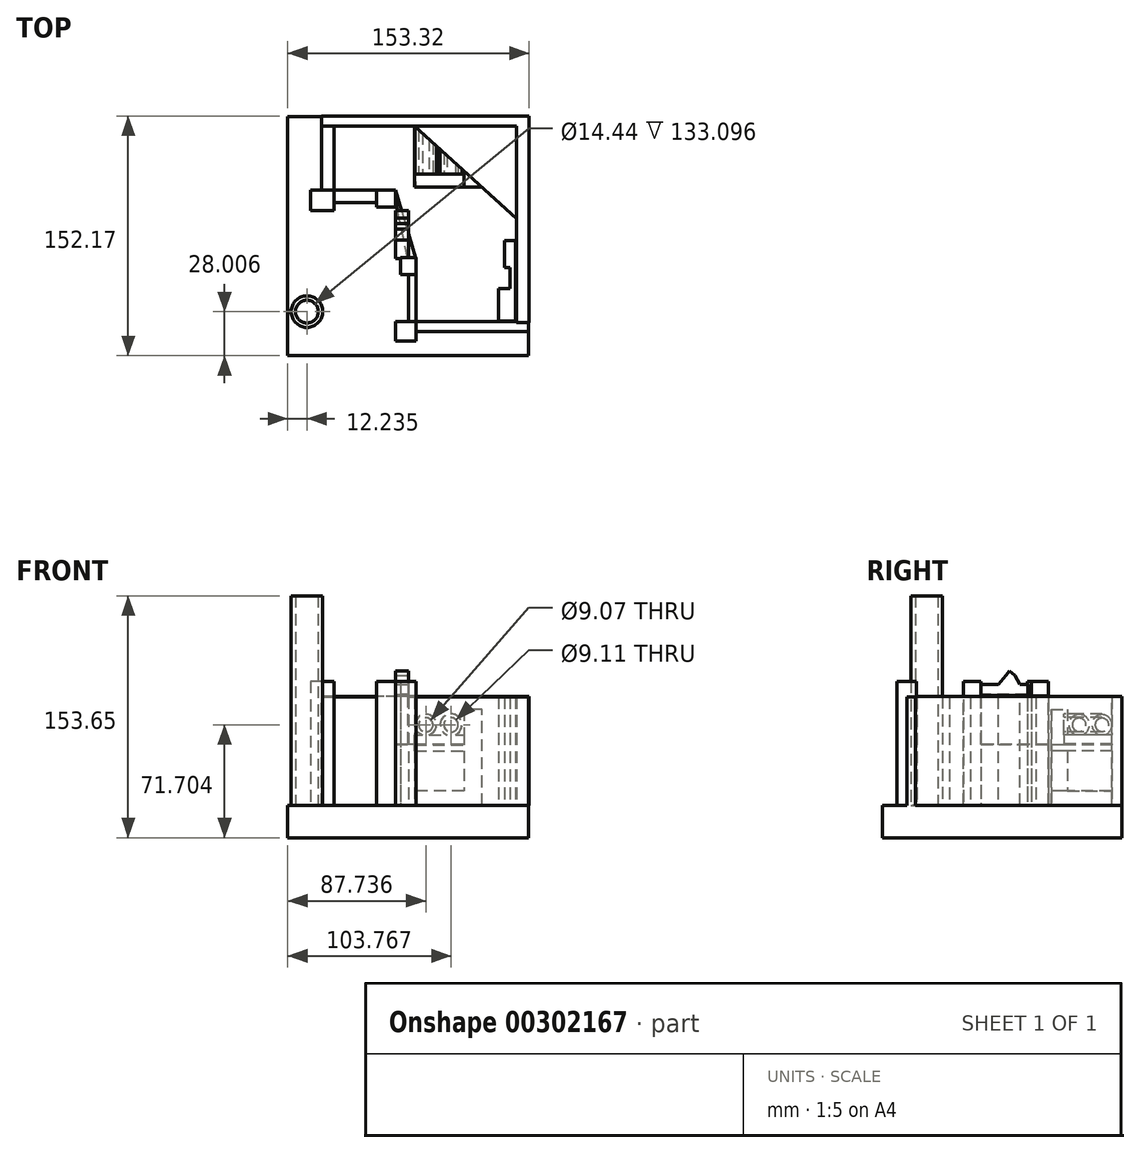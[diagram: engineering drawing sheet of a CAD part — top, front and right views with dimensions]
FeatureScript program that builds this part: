
annotation { "Feature Type Name" : "Feature", "Feature Type Description" : "" }
export const myFeature = defineFeature(function(context is Context, id is Id, definition is map)
    precondition{}
    {
        {
            var Q0;
            Q0=qCreatedBy(makeId("Front.planeOp"),FACE);
            var sketch = newSketch(context, id + "F0", { "sketchPlane" : qUnion([Q0])});
            skLineSegment(sketch, "E0.bottom", {"start": v(-76.66, 0) * mm, "end": v(76.37, 0) * mm});
            skLineSegment(sketch, "E0.top", {"start": v(-76.66, -20.55) * mm, "end": v(76.37, -20.55) * mm});
            skLineSegment(sketch, "E0.left", {"start": v(-76.66, 0) * mm, "end": v(-76.66, -20.55) * mm});
            skLineSegment(sketch, "E0.right", {"start": v(76.37, 0) * mm, "end": v(76.37, -20.55) * mm});
            skSolve(sketch);
        }
        {
            var Q0;
            Q0 = qSketchRegion(id + "F0", true);
            extrude(context, id + "F1", {"entities" : qUnion([Q0]), "depth" : 75.95 * mm, "hasSecondDirection" : true, "secondDirectionOppositeDirection" : true, "secondDirectionDepth" : 75.95 * mm});
        }
        {
            var Q0;
            Q0=makeQuery(id+"F1.opExtrude","SWEPT_FACE",FACE,{"disambiguationData":[OSD([sQuery(id+"F0.wireOp",EDGE,"E0.bottom")])]});
            var sketch = newSketch(context, id + "F2", { "sketchPlane" : qUnion([Q0])});
            skLineSegment(sketch, "E1", {"start": v(4.08, 69.8) * mm, "end": v(69.08, 69.8) * mm});
            skLineSegment(sketch, "E2", {"start": v(69.08, 69.8) * mm, "end": v(69.08, 10.93) * mm});
            skLineSegment(sketch, "E3", {"start": v(69.08, 10.93) * mm, "end": v(4.08, 69.8) * mm});
            skSolve(sketch);
        }
        {
            var Q0;
            Q0 = qSketchRegion(id + "F2", true);
            extrude(context, id + "F3", {"entities" : qUnion([Q0]), "operationType" : NewBodyOperationType.ADD, "depth" : 68.83 * mm});
        }
        {
            var Q0;
            Q0=qCreatedBy(makeId("Front.planeOp"),FACE);
            var sketch = newSketch(context, id + "F4", { "sketchPlane" : qUnion([Q0])});
            skLineSegment(sketch, "E4.bottom", {"start": v(4.08, 38.33) * mm, "end": v(35.27, 38.33) * mm});
            skLineSegment(sketch, "E4.top", {"start": v(4.08, 34.54) * mm, "end": v(35.27, 34.54) * mm});
            skLineSegment(sketch, "E4.left", {"start": v(4.08, 38.33) * mm, "end": v(4.08, 34.54) * mm});
            skLineSegment(sketch, "E4.right", {"start": v(35.27, 38.33) * mm, "end": v(35.27, 34.54) * mm});
            skLineSegment(sketch, "E5.bottom", {"start": v(68.79, 61.06) * mm, "end": v(35.27, 61.06) * mm});
            skLineSegment(sketch, "E5.top", {"start": v(68.79, 0) * mm, "end": v(35.27, 0) * mm});
            skLineSegment(sketch, "E5.left", {"start": v(68.79, 61.06) * mm, "end": v(68.79, 0) * mm});
            skLineSegment(sketch, "E5.right", {"start": v(35.27, 61.06) * mm, "end": v(35.27, 0) * mm});
            skLineSegment(sketch, "E6.bottom", {"start": v(35.27, 9.18) * mm, "end": v(4.66, 9.18) * mm});
            skLineSegment(sketch, "E6.top", {"start": v(35.27, 0) * mm, "end": v(4.66, 0) * mm});
            skLineSegment(sketch, "E6.left", {"start": v(35.27, 9.18) * mm, "end": v(35.27, 0) * mm});
            skLineSegment(sketch, "E6.right", {"start": v(4.66, 9.18) * mm, "end": v(4.66, 0) * mm});
            skSolve(sketch);
        }
        {
            var Q0;
            Q0 = qSketchRegion(id + "F4", true);
            extrude(context, id + "F5", {"entities" : qUnion([Q0]), "operationType" : NewBodyOperationType.ADD, "oppositeDirection" : true, "depth" : 70.1 * mm, "hasSecondDirection" : true, "secondDirectionOppositeDirection" : true, "secondDirectionDepth" : 31.24 * mm});
        }
        {
            var Q0;
            Q0=qCreatedBy(makeId("Front.planeOp"),FACE);
            var sketch = newSketch(context, id + "F6", { "sketchPlane" : qUnion([Q0])});
            skCircle(sketch, "E7", {"center": v(11.08, 51.15) * mm, "radius": 6.78 * mm});
            skCircle(sketch, "E8", {"center": v(11.08, 51.15) * mm, "radius": 4.53 * mm});
            skCircle(sketch, "E9", {"center": v(27.1, 51.15) * mm, "radius": 6.95 * mm});
            skCircle(sketch, "E10", {"center": v(27.1, 51.15) * mm, "radius": 4.55 * mm});
            skLineSegment(sketch, "E11.bottom", {"start": v(3.79, 44.74) * mm, "end": v(17.78, 44.74) * mm});
            skLineSegment(sketch, "E11.top", {"start": v(3.79, 38.91) * mm, "end": v(17.78, 38.91) * mm});
            skLineSegment(sketch, "E11.left", {"start": v(3.79, 44.74) * mm, "end": v(3.79, 38.91) * mm});
            skLineSegment(sketch, "E11.right", {"start": v(17.78, 44.74) * mm, "end": v(17.78, 38.91) * mm});
            skLineSegment(sketch, "E12.bottom", {"start": v(17.78, 44.74) * mm, "end": v(35.27, 44.74) * mm});
            skLineSegment(sketch, "E12.top", {"start": v(17.78, 38.91) * mm, "end": v(35.27, 38.91) * mm});
            skLineSegment(sketch, "E12.right", {"start": v(35.27, 44.74) * mm, "end": v(35.27, 38.91) * mm});
            skSolve(sketch);
        }
        {
            var Q0;
            Q0 = qSketchRegion(id + "F6", true);
            extrude(context, id + "F7", {"entities" : qUnion([Q0]), "operationType" : NewBodyOperationType.ADD, "oppositeDirection" : true, "depth" : 70.1 * mm, "hasSecondDirection" : true, "secondDirectionOppositeDirection" : true, "secondDirectionDepth" : 39.37 * mm});
        }
        {
            var Q0;
            Q0=qCreatedBy(makeId("Top.planeOp"),FACE);
            var sketch = newSketch(context, id + "F8", { "sketchPlane" : qUnion([Q0])});
            skLineSegment(sketch, "E13.bottom", {"start": v(68.79, 69.8) * mm, "end": v(76.66, 69.8) * mm});
            skLineSegment(sketch, "E13.top", {"start": v(68.79, -54.94) * mm, "end": v(76.66, -54.94) * mm});
            skLineSegment(sketch, "E13.left", {"start": v(68.79, 69.8) * mm, "end": v(68.79, -54.94) * mm});
            skLineSegment(sketch, "E13.right", {"start": v(76.66, 69.8) * mm, "end": v(76.66, -54.94) * mm});
            skLineSegment(sketch, "E14.bottom", {"start": v(76.66, 69.8) * mm, "end": v(-55.09, 69.8) * mm});
            skLineSegment(sketch, "E14.top", {"start": v(76.66, 76.22) * mm, "end": v(-55.09, 76.22) * mm});
            skLineSegment(sketch, "E14.left", {"start": v(76.66, 69.8) * mm, "end": v(76.66, 76.22) * mm});
            skLineSegment(sketch, "E14.right", {"start": v(-55.09, 69.8) * mm, "end": v(-55.09, 76.22) * mm});
            skSolve(sketch);
        }
        {
            var Q0;
            Q0 = qSketchRegion(id + "F8", true);
            extrude(context, id + "F9", {"entities" : qUnion([Q0]), "operationType" : NewBodyOperationType.ADD, "depth" : 69.1 * mm});
        }
        {
            var Q0;
            Q0=qCreatedBy(makeId("Top.planeOp"),FACE);
            var sketch = newSketch(context, id + "F10", { "sketchPlane" : qUnion([Q0])});
            skLineSegment(sketch, "E15.bottom", {"start": v(67.91, -2.77) * mm, "end": v(60.92, -2.77) * mm});
            skLineSegment(sketch, "E15.top", {"start": v(67.91, -19.97) * mm, "end": v(60.92, -19.97) * mm});
            skLineSegment(sketch, "E15.left", {"start": v(67.91, -2.77) * mm, "end": v(67.91, -19.97) * mm});
            skLineSegment(sketch, "E15.right", {"start": v(60.92, -2.77) * mm, "end": v(60.92, -19.97) * mm});
            skPoint(sketch, "E16.oppositeSnap0", {"position": v(64.42, -19.97) * mm});
            skLineSegment(sketch, "E16.bottom", {"start": v(67.91, -19.97) * mm, "end": v(64.42, -19.97) * mm});
            skLineSegment(sketch, "E16.top", {"start": v(67.91, -33.37) * mm, "end": v(64.42, -33.37) * mm});
            skLineSegment(sketch, "E16.left", {"start": v(67.91, -19.97) * mm, "end": v(67.91, -33.37) * mm});
            skLineSegment(sketch, "E16.right", {"start": v(64.42, -19.97) * mm, "end": v(64.42, -33.37) * mm});
            skLineSegment(sketch, "E17.bottom", {"start": v(67.91, -33.37) * mm, "end": v(57.13, -33.37) * mm});
            skLineSegment(sketch, "E17.top", {"start": v(67.91, -54.07) * mm, "end": v(57.13, -54.07) * mm});
            skLineSegment(sketch, "E17.left", {"start": v(67.91, -33.37) * mm, "end": v(67.91, -54.07) * mm});
            skLineSegment(sketch, "E17.right", {"start": v(57.13, -33.37) * mm, "end": v(57.13, -54.07) * mm});
            skSolve(sketch);
        }
        {
            var Q0;
            Q0 = qSketchRegion(id + "F10", true);
            extrude(context, id + "F11", {"entities" : qUnion([Q0]), "operationType" : NewBodyOperationType.ADD, "depth" : 68.83 * mm});
        }
        {
            var Q0;
            Q0=qCreatedBy(makeId("Top.planeOp"),FACE);
            var sketch = newSketch(context, id + "F12", { "sketchPlane" : qUnion([Q0])});
            skLineSegment(sketch, "E18.bottom", {"start": v(76.37, -54.36) * mm, "end": v(0, -54.36) * mm});
            skLineSegment(sketch, "E18.top", {"start": v(76.37, -60.48) * mm, "end": v(0, -60.48) * mm});
            skLineSegment(sketch, "E18.left", {"start": v(76.37, -54.36) * mm, "end": v(76.37, -60.48) * mm});
            skLineSegment(sketch, "E18.right", {"start": v(0, -54.36) * mm, "end": v(0, -60.48) * mm});
            skLineSegment(sketch, "E19.bottom", {"start": v(-55.09, 75.93) * mm, "end": v(-47.22, 75.93) * mm});
            skLineSegment(sketch, "E19.top", {"start": v(-55.09, 21.42) * mm, "end": v(-47.22, 21.42) * mm});
            skLineSegment(sketch, "E19.left", {"start": v(-55.09, 75.93) * mm, "end": v(-55.09, 21.42) * mm});
            skLineSegment(sketch, "E19.right", {"start": v(-47.22, 75.93) * mm, "end": v(-47.22, 21.42) * mm});
            skLineSegment(sketch, "E20.bottom", {"start": v(-47.22, 21.42) * mm, "end": v(-8.16, 21.42) * mm});
            skLineSegment(sketch, "E20.top", {"start": v(-47.22, 29.3) * mm, "end": v(-8.16, 29.3) * mm});
            skLineSegment(sketch, "E20.left", {"start": v(-47.22, 21.42) * mm, "end": v(-47.22, 29.3) * mm});
            skLineSegment(sketch, "E20.right", {"start": v(-8.16, 21.42) * mm, "end": v(-8.16, 29.3) * mm});
            skLineSegment(sketch, "E21.bottom", {"start": v(0, -54.36) * mm, "end": v(4.96, -54.36) * mm});
            skLineSegment(sketch, "E21.top", {"start": v(0, -15.3) * mm, "end": v(4.96, -15.3) * mm});
            skLineSegment(sketch, "E21.left", {"start": v(0, -54.36) * mm, "end": v(0, -15.3) * mm});
            skLineSegment(sketch, "E21.right", {"start": v(4.96, -54.36) * mm, "end": v(4.96, -15.3) * mm});
            skSolve(sketch);
        }
        {
            var Q0;
            Q0 = qSketchRegion(id + "F12", true);
            extrude(context, id + "F13", {"entities" : qUnion([Q0]), "operationType" : NewBodyOperationType.ADD, "depth" : 68.83 * mm});
        }
        {
            var Q0;
            Q0=makeQuery(id+"F1.opExtrude","SWEPT_FACE",FACE,{"disambiguationData":[OSD([sQuery(id+"F0.wireOp",EDGE,"E0.bottom")])]});
            var sketch = newSketch(context, id + "F14", { "sketchPlane" : qUnion([Q0])});
            skLineSegment(sketch, "E22", {"start": v(-8.16, 29.3) * mm, "end": v(4.96, -15.3) * mm});
            skLineSegment(sketch, "E23", {"start": v(0, -15.3) * mm, "end": v(-8.16, 21.42) * mm});
            skLineSegment(sketch, "E24", {"start": v(-8.16, 21.42) * mm, "end": v(-8.16, 29.3) * mm});
            skLineSegment(sketch, "E25", {"start": v(0, -15.3) * mm, "end": v(4.96, -15.3) * mm});
            skSolve(sketch);
        }
        {
            var Q0;
            Q0 = qSketchRegion(id + "F14", true);
            extrude(context, id + "F15", {"entities" : qUnion([Q0]), "operationType" : NewBodyOperationType.ADD, "depth" : 69.6 * mm, "hasSecondDirection" : true, "secondDirectionOppositeDirection" : false, "secondDirectionDepth" : 38.6 * mm});
        }
        {
            var Q0;
            Q0=makeQuery(id+"F1.opExtrude","SWEPT_FACE",FACE,{"disambiguationData":[OSD([sQuery(id+"F0.wireOp",EDGE,"E0.bottom")])]});
            var sketch = newSketch(context, id + "F16", { "sketchPlane" : qUnion([Q0])});
            skLineSegment(sketch, "E26.bottom", {"start": v(-4.84, -13.5) * mm, "end": v(4.96, -13.5) * mm});
            skLineSegment(sketch, "E26.top", {"start": v(-4.84, -24.42) * mm, "end": v(4.96, -24.42) * mm});
            skLineSegment(sketch, "E26.left", {"start": v(-4.84, -13.5) * mm, "end": v(-4.84, -24.42) * mm});
            skLineSegment(sketch, "E26.right", {"start": v(4.96, -13.5) * mm, "end": v(4.96, -24.42) * mm});
            skLineSegment(sketch, "E27.bottom", {"start": v(-8.16, 29.3) * mm, "end": v(-20.3, 29.3) * mm});
            skLineSegment(sketch, "E27.top", {"start": v(-8.16, 18.46) * mm, "end": v(-20.3, 18.46) * mm});
            skLineSegment(sketch, "E27.left", {"start": v(-8.16, 29.3) * mm, "end": v(-8.16, 18.46) * mm});
            skLineSegment(sketch, "E27.right", {"start": v(-20.3, 29.3) * mm, "end": v(-20.3, 18.46) * mm});
            skLineSegment(sketch, "E28.bottom", {"start": v(-47.22, 29.3) * mm, "end": v(-62.15, 29.3) * mm});
            skLineSegment(sketch, "E28.top", {"start": v(-47.22, 16.2) * mm, "end": v(-62.15, 16.2) * mm});
            skLineSegment(sketch, "E28.left", {"start": v(-47.22, 29.3) * mm, "end": v(-47.22, 16.2) * mm});
            skLineSegment(sketch, "E28.right", {"start": v(-62.15, 29.3) * mm, "end": v(-62.15, 16.2) * mm});
            skLineSegment(sketch, "E29.bottom", {"start": v(4.96, -54.36) * mm, "end": v(-8.16, -54.36) * mm});
            skLineSegment(sketch, "E29.top", {"start": v(4.96, -66.67) * mm, "end": v(-8.16, -66.67) * mm});
            skLineSegment(sketch, "E29.left", {"start": v(4.96, -54.36) * mm, "end": v(4.96, -66.67) * mm});
            skLineSegment(sketch, "E29.right", {"start": v(-8.16, -54.36) * mm, "end": v(-8.16, -66.67) * mm});
            skSolve(sketch);
        }
        {
            var Q0;
            Q0 = qSketchRegion(id + "F16", true);
            extrude(context, id + "F17", {"entities" : qUnion([Q0]), "operationType" : NewBodyOperationType.ADD, "depth" : 78.74 * mm});
        }
        {
            var Q0;
            Q0=qCreatedBy(makeId("Right.planeOp"),FACE);
            var sketch = newSketch(context, id + "F18", { "sketchPlane" : qUnion([Q0])});
            skLineSegment(sketch, "E30", {"start": v(16.16, 76.9) * mm, "end": v(11.38, 76.9) * mm});
            skLineSegment(sketch, "E31", {"start": v(11.38, 76.9) * mm, "end": v(8, 82.53) * mm});
            skLineSegment(sketch, "E32", {"start": v(8, 82.53) * mm, "end": v(4.63, 85.34) * mm});
            skLineSegment(sketch, "E33", {"start": v(4.63, 85.34) * mm, "end": v(2.28, 82.53) * mm});
            skLineSegment(sketch, "E34", {"start": v(2.28, 82.53) * mm, "end": v(-2.41, 76.9) * mm});
            skLineSegment(sketch, "E35", {"start": v(-2.41, 76.9) * mm, "end": v(-14.23, 76.9) * mm});
            skLineSegment(sketch, "E36", {"start": v(-14.23, 76.9) * mm, "end": v(-14.23, 70.42) * mm});
            skLineSegment(sketch, "E37", {"start": v(-14.23, 70.42) * mm, "end": v(15.88, 70.42) * mm});
            skLineSegment(sketch, "E38", {"start": v(15.88, 70.42) * mm, "end": v(16.16, 76.9) * mm});
            skSolve(sketch);
        }
        {
            var Q0;
            Q0 = qSketchRegion(id + "F18", true);
            extrude(context, id + "F19", {"entities" : qUnion([Q0]), "operationType" : NewBodyOperationType.ADD, "oppositeDirection" : true, "depth" : 8.13 * mm});
        }
        {
            var Q0;
            Q0=qCreatedBy(makeId("Top.planeOp"),FACE);
            var sketch = newSketch(context, id + "F20", { "sketchPlane" : qUnion([Q0])});
            skCircle(sketch, "E39", {"center": v(-64.42, -47.94) * mm, "radius": 10.03 * mm});
            skCircle(sketch, "E40", {"center": v(-64.42, -47.94) * mm, "radius": 7.22 * mm});
            skSolve(sketch);
        }
        {
            var Q0;
            Q0 = qSketchRegion(id + "F20", true);
            extrude(context, id + "F21", {"entities" : qUnion([Q0]), "operationType" : NewBodyOperationType.ADD, "depth" : 133.1 * mm});
        }
        {
            var Q0;
            Q0=qCreatedBy(makeId("Right.planeOp"),FACE);
            var sketch = newSketch(context, id + "F22", { "sketchPlane" : qUnion([Q0])});
            skLineSegment(sketch, "E41.bottom", {"start": v(16.3, 76.93) * mm, "end": v(15.26, 76.93) * mm});
            skLineSegment(sketch, "E41.top", {"start": v(16.3, 69.66) * mm, "end": v(15.26, 69.66) * mm});
            skLineSegment(sketch, "E41.left", {"start": v(16.3, 76.93) * mm, "end": v(16.3, 69.66) * mm});
            skLineSegment(sketch, "E41.right", {"start": v(15.26, 76.93) * mm, "end": v(15.26, 69.66) * mm});
            skLineSegment(sketch, "E42.bottom", {"start": v(15.26, 69.66) * mm, "end": v(-14.2, 69.66) * mm});
            skLineSegment(sketch, "E42.top", {"start": v(15.26, 70.62) * mm, "end": v(-14.2, 70.62) * mm});
            skLineSegment(sketch, "E42.left", {"start": v(15.26, 69.66) * mm, "end": v(15.26, 70.62) * mm});
            skLineSegment(sketch, "E42.right", {"start": v(-14.2, 69.66) * mm, "end": v(-14.2, 70.62) * mm});
            skSolve(sketch);
        }
        {
            var Q0;
            Q0 = qSketchRegion(id + "F22", true);
            extrude(context, id + "F23", {"entities" : qUnion([Q0]), "operationType" : NewBodyOperationType.ADD, "oppositeDirection" : true, "depth" : 0.25 * mm});
        }
    });
